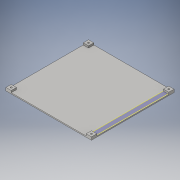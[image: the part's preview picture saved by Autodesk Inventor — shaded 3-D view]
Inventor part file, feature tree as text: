
AUTODESK INVENTOR PART (.ipt)
format: ipt  version: 2016 SP2 (Build 200236200, 236)  size: 165,888 bytes
history: native  units: mm
features: extrude x4, sketch x4, reference x2, plane x1, projected_geometry x1
ambient origin geometry x8: Origin, YZ Plane, XZ Plane, XY Plane, X Axis, Y Axis, Z Axis, Center Point
bodies: Volumenkörper1 (feature_tree)
feature tree (12):
  plane  "Arbeitsebene1"
  extrude  "Extrusion1"  Depth=3.5mm TaperAngle=0.0deg
  extrude  "Extrusion2"  Depth=3.1mm TaperAngle=0.0deg
  extrude  "Extrusion3"  Depth=0.1mm
  extrude  "Extrusion4"  Depth=5.7mm
  sketch  "Skizze1"  dims[d0=2.0mm d1=0.0mm d10=3.5mm d11=0.0mm]
  reference  "Referenz1"
  reference  "Referenz2"
  sketch  "Skizze2"  dims[d12=15.5mm d13=0.0mm d18=3.1mm d19=0.0mm]
  sketch  "Skizze3"  dims[d24=0.1mm d25=0.1mm]
  sketch  "Skizze4"  dims[d27=5.7mm d28=5.7mm d29=5.7mm d30=5.7mm]
  projected_geometry  "Projizierte Kontur1"
